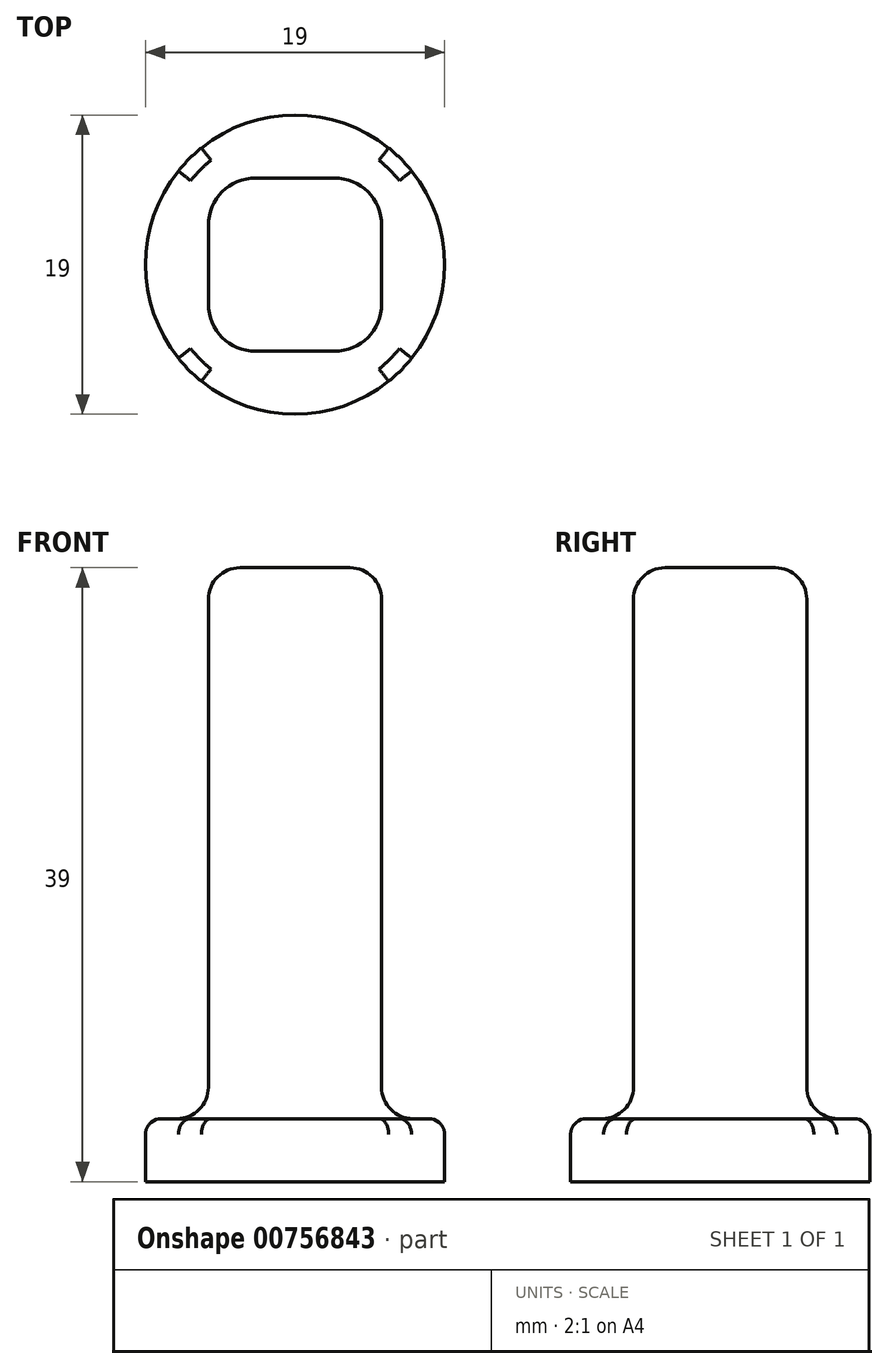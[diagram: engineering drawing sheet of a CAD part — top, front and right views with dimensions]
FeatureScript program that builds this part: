
annotation { "Feature Type Name" : "Feature", "Feature Type Description" : "" }
export const myFeature = defineFeature(function(context is Context, id is Id, definition is map)
    precondition{}
    {
        {
            var Q0;
            Q0=qCreatedBy(makeId("Top.planeOp"),FACE);
            var sketch = newSketch(context, id + "F0", { "sketchPlane" : qUnion([Q0])});
            skCircle(sketch, "E0", {"center": v(0, 0) * mm, "radius": 9.5 * mm});
            skSolve(sketch);
        }
        {
            var Q0;
            Q0=makeQuery(id+"F0.imprint","IMPRINT",FACE,{"disambiguationData":[TD([[makeQuery(id+"F0.imprint","IMPRINT",EDGE,{"derivedFrom":sQuery(id+"F0.wireOp",EDGE,"E0")}),1.0]])]});
            extrude(context, id + "F1", {"entities" : qUnion([Q0]), "depth" : 4 * mm, "offsetDistance" : 25 * mm});
        }
        {
            var Q0;
            Q0=makeQuery(id+"F1.opExtrude","CAP_FACE",FACE,{"disambiguationData":[OSD([sQuery(id+"F0.wireOp",EDGE,"E0")])],"isStart":false});
            var sketch = newSketch(context, id + "F2", { "sketchPlane" : qUnion([Q0])});
            skLineSegment(sketch, "E1.bottom", {"start": v(5.5, -5.5) * mm, "end": v(-5.5, -5.5) * mm});
            skLineSegment(sketch, "E1.top", {"start": v(5.5, 5.5) * mm, "end": v(-5.5, 5.5) * mm});
            skLineSegment(sketch, "E1.left", {"start": v(5.5, -5.5) * mm, "end": v(5.5, 5.5) * mm});
            skLineSegment(sketch, "E1.right", {"start": v(-5.5, -5.5) * mm, "end": v(-5.5, 5.5) * mm});
            skPoint(sketch, "E1.middle", {"position": v(0, 0) * mm});
            skSolve(sketch);
        }
        {
            var Q0;
            Q0=makeQuery(id+"F2.imprint","IMPRINT",FACE,{"disambiguationData":[TD([[makeQuery(id+"F2.imprint","IMPRINT",EDGE,{"derivedFrom":sQuery(id+"F2.wireOp",EDGE,"E1.bottom")}),-1.0]])]});
            extrude(context, id + "F3", {"entities" : qUnion([Q0]), "operationType" : NewBodyOperationType.ADD, "depth" : 35 * mm, "offsetDistance" : 25 * mm});
        }
        {
            var Q0;
            Q0=makeQuery(id+"F3.opExtrude","SWEPT_FACE",FACE,{"disambiguationData":[OSD([sQuery(id+"F2.wireOp",EDGE,"E1.left")])]});
            var sketch = newSketch(context, id + "F4", { "sketchPlane" : qUnion([Q0])});
            skLineSegment(sketch, "E2", {"start": v(5.5, 21.5) * mm, "end": v(-5.5, 21.5) * mm, "construction": true});
            skSolve(sketch);
        }
        {
            var Q0;
            Q0=qCreatedBy(makeId("Top.planeOp"),FACE);
            var Q1;
            Q1=sQuery(id+"F4.wireOp",EDGE,"E2");
            cPlane(context, id + "F5", {"entities" : qUnion([Q0, Q1]), "cplaneType" : CPlaneType.LINE_ANGLE, "offset" : 25 * mm, "angle" : 0 * degree, "width" : 150 * mm, "height" : 150 * mm});
        }
        {
            var Q0;
            Q0=makeQuery(id+"F3.opExtrude","SWEPT_EDGE",EDGE,{"disambiguationData":[OSD([sQuery(id+"F2.wireOp",EDGE,"E1.bottom"),sQuery(id+"F2.wireOp",EDGE,"E1.left")])]});
            var Q1;
            Q1=makeQuery(id+"F3.opExtrude","SWEPT_EDGE",EDGE,{"disambiguationData":[OSD([sQuery(id+"F2.wireOp",EDGE,"E1.top"),sQuery(id+"F2.wireOp",EDGE,"E1.left")])]});
            var Q2;
            Q2=makeQuery(id+"F3.opExtrude","SWEPT_EDGE",EDGE,{"disambiguationData":[OSD([sQuery(id+"F2.wireOp",EDGE,"E1.bottom"),sQuery(id+"F2.wireOp",EDGE,"E1.right")])]});
            var Q3;
            Q3=makeQuery(id+"F3.opExtrude","SWEPT_EDGE",EDGE,{"disambiguationData":[OSD([sQuery(id+"F2.wireOp",EDGE,"E1.top"),sQuery(id+"F2.wireOp",EDGE,"E1.right")])]});
            fillet(context, id + "F6", {"entities" : qUnion([Q0, Q1, Q2, Q3]), "radius" : 3 * mm, "tangentPropagation" : true, "allowEdgeOverflow" : false});
        }
        {
            var Q0;
            Q0=makeQuery(id+"F3.opExtrude","SWEPT_FACE",FACE,{"disambiguationData":[OSD([sQuery(id+"F2.wireOp",EDGE,"E1.top")])]});
            var Q1;
            Q1=makeQuery(id+"F6.opFillet","BLEND_EDGE",EDGE,{"blendedFrom":[makeQuery(id+"F3.opExtrude","SWEPT_EDGE",EDGE,{"disambiguationData":[OSD([sQuery(id+"F2.wireOp",EDGE,"E1.top"),sQuery(id+"F2.wireOp",EDGE,"E1.left")])]}),makeQuery(id+"F1.opExtrude","CAP_FACE",FACE,{"disambiguationData":[OSD([sQuery(id+"F0.wireOp",EDGE,"E0")])],"isStart":false})],"blendedInto":[makeQuery(id+"F1.opExtrude","CAP_FACE",FACE,{"disambiguationData":[OSD([sQuery(id+"F0.wireOp",EDGE,"E0")])],"isStart":false})]});
            fillet(context, id + "F7", {"entities" : qUnion([Q0, Q1]), "radius" : 2 * mm, "tangentPropagation" : true, "allowEdgeOverflow" : false});
        }
        {
            var Q0;
            Q0=makeQuery(id+"F1.opExtrude","CAP_EDGE",EDGE,{"disambiguationData":[OSD([sQuery(id+"F0.wireOp",EDGE,"E0")])],"isStart":false});
            var Q1;
            Q1=makeQuery(id+"Fn5yIeiJ8zzVRFC_1.1.F1.opExtrude","CAP_EDGE",EDGE,{"disambiguationData":[OSD([sQuery(id+"F0.wireOp",EDGE,"E0")])],"isStart":false});
            fillet(context, id + "F8", {"entities" : qUnion([Q0, Q1]), "radius" : 1 * mm, "tangentPropagation" : true, "allowEdgeOverflow" : false});
        }
    });
